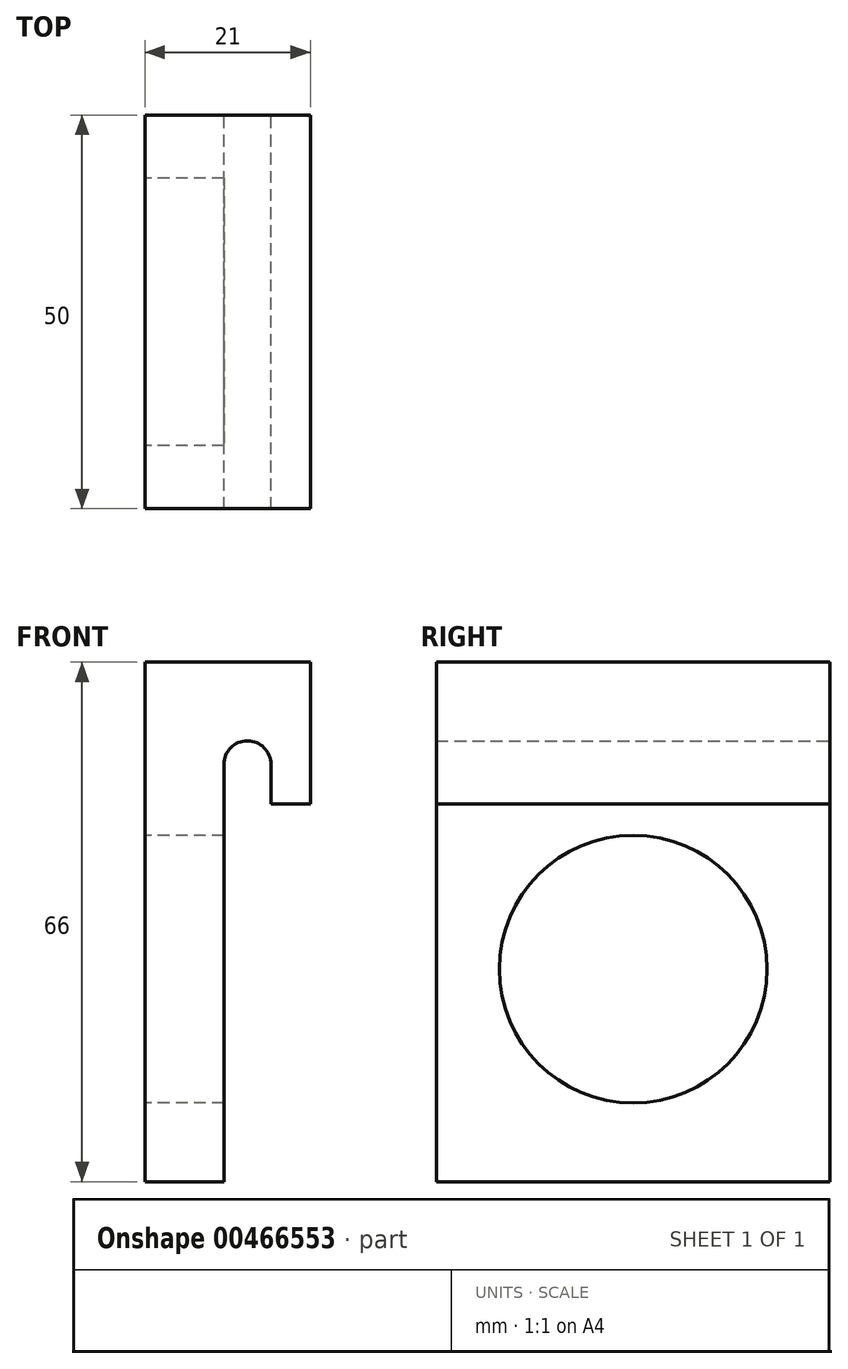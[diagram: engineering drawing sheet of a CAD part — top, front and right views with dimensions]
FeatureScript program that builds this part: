
annotation { "Feature Type Name" : "Feature", "Feature Type Description" : "" }
export const myFeature = defineFeature(function(context is Context, id is Id, definition is map)
    precondition{}
    {
        {
            var Q0;
            Q0=qCreatedBy(makeId("Front.planeOp"),FACE);
            var sketch = newSketch(context, id + "F0", { "sketchPlane" : qUnion([Q0])});
            skLineSegment(sketch, "E0.bottom", {"start": v(0, 0) * mm, "end": v(-10, 0) * mm});
            skLineSegment(sketch, "E0.top", {"start": v(0, 66) * mm, "end": v(-10, 66) * mm});
            skLineSegment(sketch, "E0.left", {"start": v(0, 0) * mm, "end": v(0, 66) * mm});
            skLineSegment(sketch, "E0.right", {"start": v(-10, 0) * mm, "end": v(-10, 66) * mm});
            skLineSegment(sketch, "E1.bottom", {"start": v(0, 66) * mm, "end": v(6, 66) * mm});
            skLineSegment(sketch, "E1.left", {"start": v(0, 66) * mm, "end": v(0, 53) * mm});
            skLineSegment(sketch, "E1.right", {"start": v(6, 66) * mm, "end": v(6, 53) * mm});
            skLineSegment(sketch, "E2.bottom", {"start": v(6, 66) * mm, "end": v(11, 66) * mm});
            skLineSegment(sketch, "E2.top", {"start": v(6, 48) * mm, "end": v(11, 48) * mm});
            skLineSegment(sketch, "E2.left", {"start": v(6, 66) * mm, "end": v(6, 48) * mm});
            skLineSegment(sketch, "E2.right", {"start": v(11, 66) * mm, "end": v(11, 48) * mm});
            skArc(sketch, "E3", {"start": v(6, 53) * mm, "mid": v(3, 56) * mm, "end": v(0, 53) * mm});
            skSolve(sketch);
        }
        {
            var Q0;
            Q0=qSketchRegion(id+"F0",true);
            extrude(context, id + "F1", {"entities" : qUnion([Q0]), "endBound" : BoundingType.SYMMETRIC, "depth" : 50 * mm, "offsetDistance" : 25 * mm});
        }
        {
            var Q0;
            Q0=makeQuery(id+"F1.opExtrude","SWEPT_FACE",FACE,{"disambiguationData":[OSD([sQuery(id+"F0.wireOp",EDGE,"E0.right")])]});
            var sketch = newSketch(context, id + "F2", { "sketchPlane" : qUnion([Q0])});
            skCircle(sketch, "E4", {"center": v(0, 27) * mm, "radius": 17 * mm});
            skSolve(sketch);
        }
        {
            var Q0;
            Q0=qSketchRegion(id+"F2",true);
            extrude(context, id + "F3", {"entities" : qUnion([Q0]), "operationType" : NewBodyOperationType.REMOVE, "endBound" : BoundingType.UP_TO_NEXT, "oppositeDirection" : true, "depth" : 25 * mm, "offsetDistance" : 25 * mm});
        }
    });
